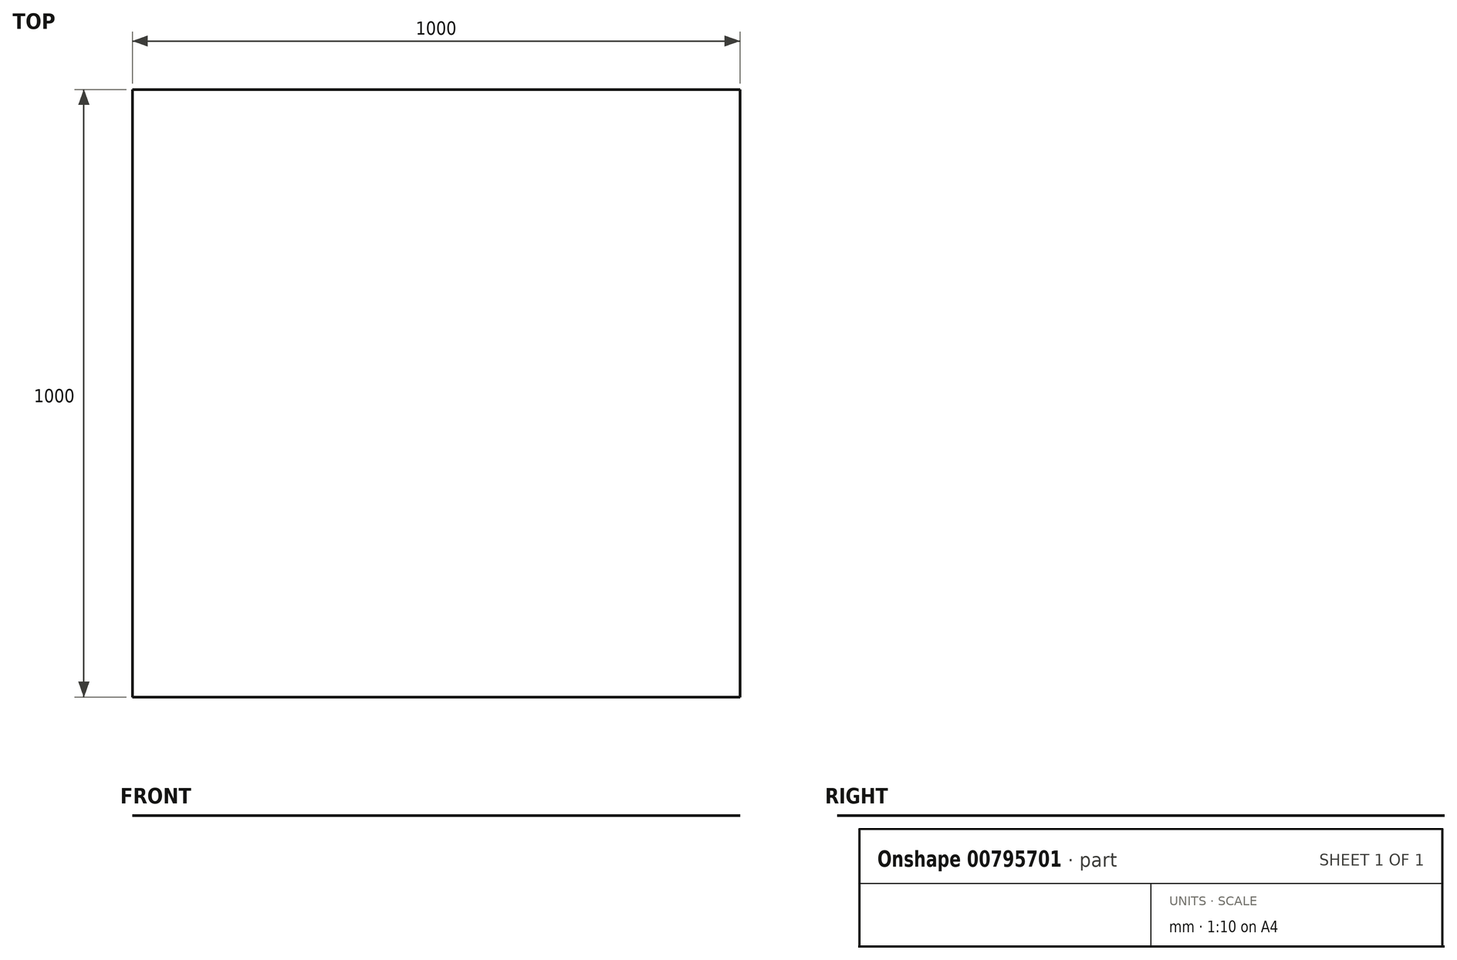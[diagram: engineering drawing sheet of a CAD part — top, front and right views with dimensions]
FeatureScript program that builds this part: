
annotation { "Feature Type Name" : "Feature", "Feature Type Description" : "" }
export const myFeature = defineFeature(function(context is Context, id is Id, definition is map)
    precondition{}
    {
        {
            var Q0;
            Q0=qCreatedBy(makeId("Front.planeOp"),FACE);
            var sketch = newSketch(context, id + "F0", { "sketchPlane" : qUnion([Q0])});
            skLineSegment(sketch, "E0", {"start": v(0, 0) * mm, "end": v(1000, 0) * mm});
            skSolve(sketch);
        }
        {
            var Q0;
            Q0=sQuery(id+"F0.wireOp",EDGE,"E0");
            extrude(context, id + "F1", {"bodyType" : ToolBodyType.SURFACE, "surfaceEntities" : qUnion([Q0]), "oppositeDirection" : true, "depth" : 1000 * mm, "offsetDistance" : 25 * mm});
        }
    });
